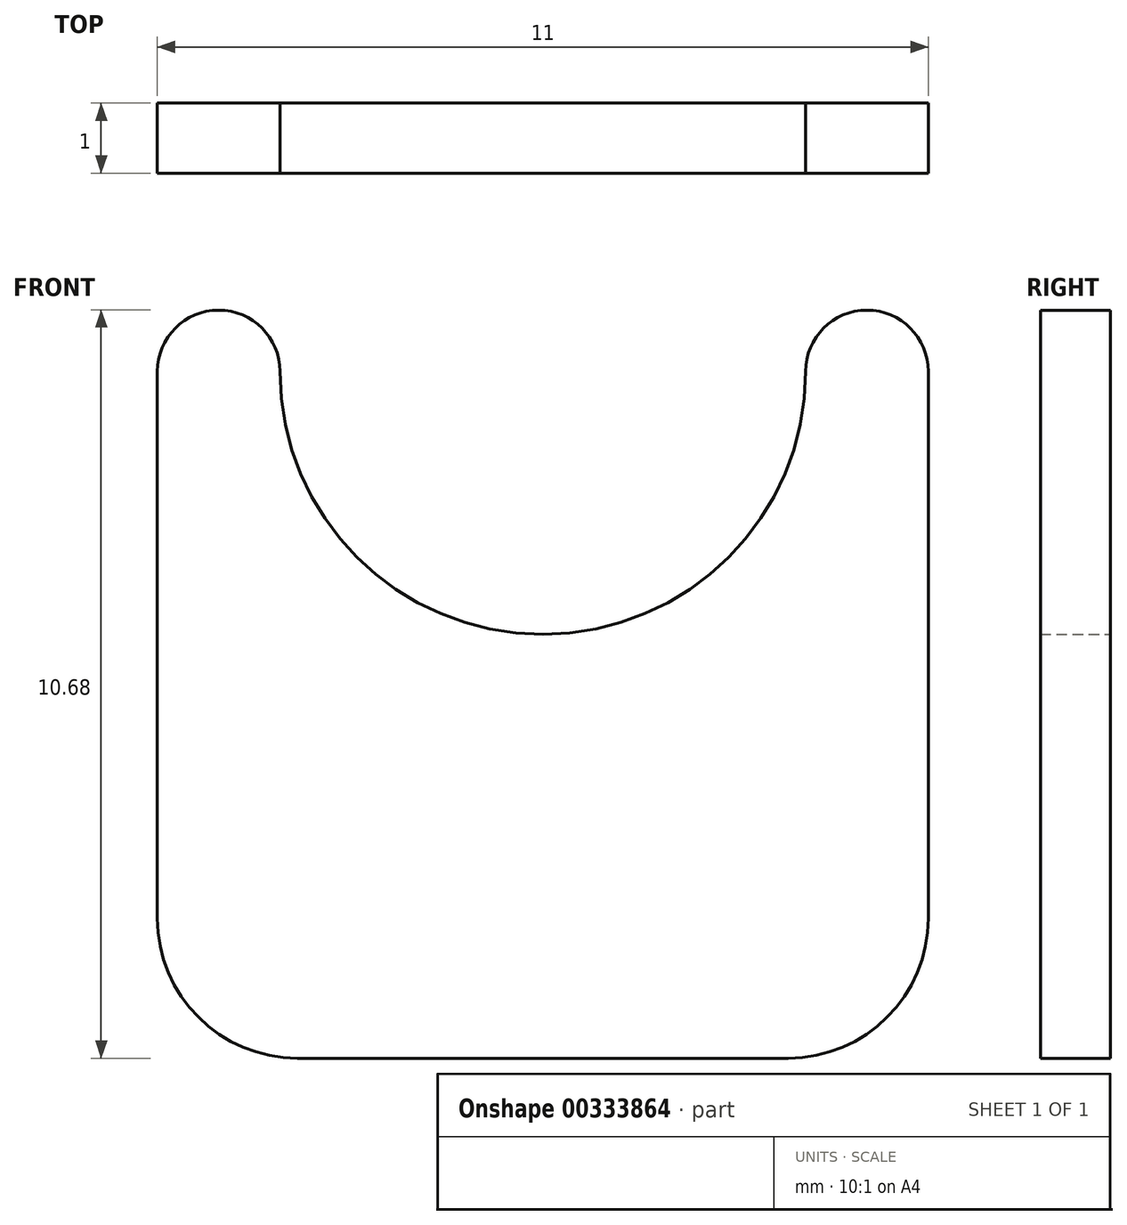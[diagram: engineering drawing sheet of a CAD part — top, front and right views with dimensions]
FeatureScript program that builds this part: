
annotation { "Feature Type Name" : "Feature", "Feature Type Description" : "" }
export const myFeature = defineFeature(function(context is Context, id is Id, definition is map)
    precondition{}
    {
        {
            var Q0;
            Q0=qCreatedBy(makeId("Front.planeOp"),FACE);
            var sketch = newSketch(context, id + "F0", { "sketchPlane" : qUnion([Q0])});
            skArc(sketch, "E0", {"start": v(-3.75, 0) * mm, "mid": v(0, -3.75) * mm, "end": v(3.75, 0) * mm});
            skLineSegment(sketch, "E1", {"start": v(5.5, 0) * mm, "end": v(5.5, -9.8) * mm});
            skLineSegment(sketch, "E2", {"start": v(5.5, -9.8) * mm, "end": v(0, -9.8) * mm});
            skLineSegment(sketch, "E3", {"start": v(-5.5, 0) * mm, "end": v(-5.5, -9.8) * mm});
            skLineSegment(sketch, "E4", {"start": v(-5.5, -9.8) * mm, "end": v(0, -9.8) * mm});
            skArc(sketch, "E5", {"start": v(-3.75, 0) * mm, "mid": v(-4.62, 0.87) * mm, "end": v(-5.5, 0) * mm});
            skArc(sketch, "E6", {"start": v(5.5, 0) * mm, "mid": v(4.62, 0.88) * mm, "end": v(3.75, 0) * mm});
            skSolve(sketch);
        }
        {
            var Q0;
            Q0 = qSketchRegion(id + "F0", true);
            extrude(context, id + "F1", {"entities" : qUnion([Q0]), "depth" : 1 * mm});
        }
        {
            var Q0;
            Q0=makeQuery(id+"F1.opExtrude","SWEPT_EDGE",EDGE,{"disambiguationData":[OSD([sQuery(id+"F0.wireOp",EDGE,"E3"),sQuery(id+"F0.wireOp",EDGE,"E4")])]});
            var Q1;
            Q1=makeQuery(id+"F1.opExtrude","SWEPT_EDGE",EDGE,{"disambiguationData":[OSD([sQuery(id+"F0.wireOp",EDGE,"E1"),sQuery(id+"F0.wireOp",EDGE,"E2")])]});
            fillet(context, id + "F2", {"entities" : qUnion([Q0, Q1]), "radius" : 2 * mm, "tangentPropagation" : true, "allowEdgeOverflow" : false});
        }
    });
